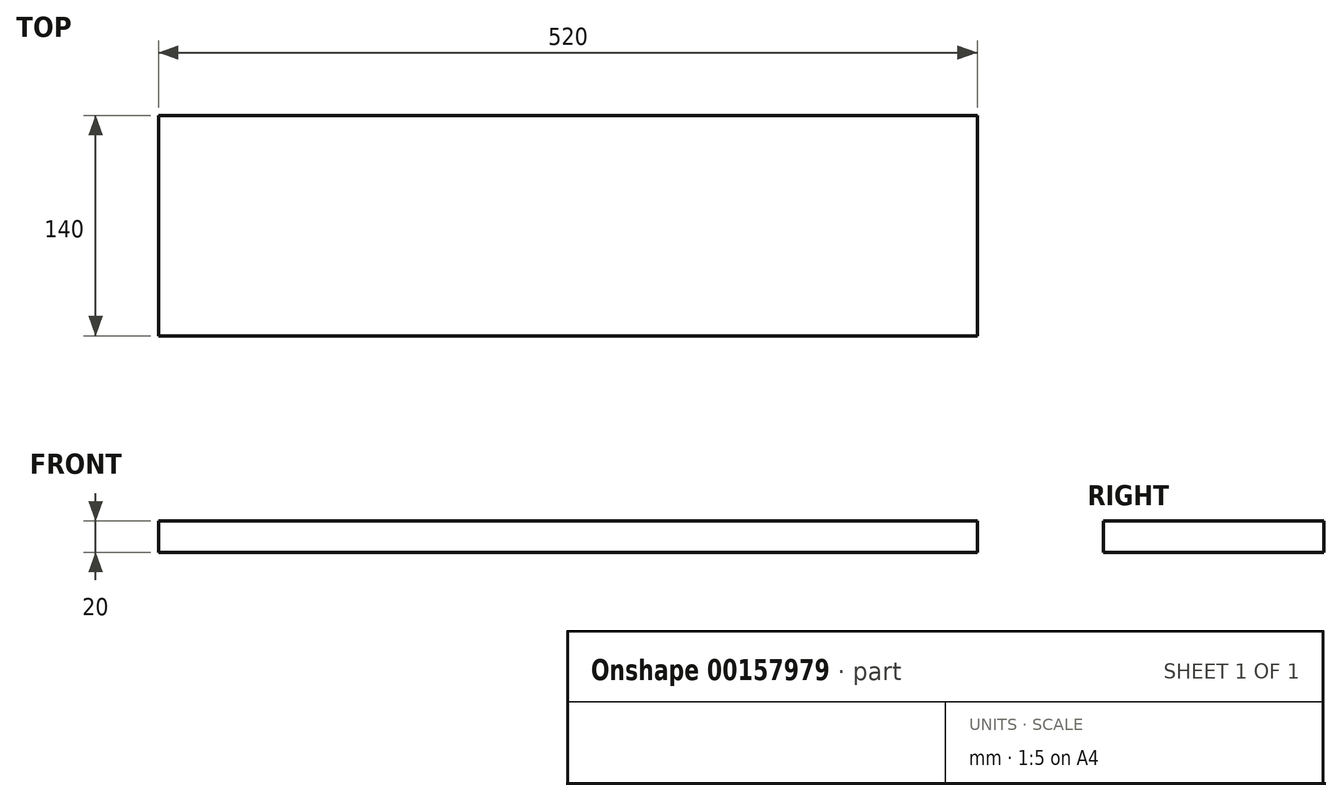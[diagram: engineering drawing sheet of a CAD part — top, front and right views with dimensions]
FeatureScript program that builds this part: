
annotation { "Feature Type Name" : "Feature", "Feature Type Description" : "" }
export const myFeature = defineFeature(function(context is Context, id is Id, definition is map)
    precondition{}
    {
        {
            var Q0;
            Q0=qCreatedBy(makeId("Top.planeOp"),FACE);
            var sketch = newSketch(context, id + "F0", { "sketchPlane" : qUnion([Q0])});
            skLineSegment(sketch, "E0.bottom", {"start": v(-260, -70) * mm, "end": v(260, -70) * mm});
            skLineSegment(sketch, "E0.top", {"start": v(-260, 70) * mm, "end": v(260, 70) * mm});
            skLineSegment(sketch, "E0.left", {"start": v(-260, -70) * mm, "end": v(-260, 70) * mm});
            skLineSegment(sketch, "E0.right", {"start": v(260, -70) * mm, "end": v(260, 70) * mm});
            skPoint(sketch, "E0.middle", {"position": v(0, 0) * mm});
            skSolve(sketch);
        }
        {
            var Q0;
            Q0=qSketchRegion(id+"F0",true);
            extrude(context, id + "F1", {"entities" : qUnion([Q0]), "endBound" : BoundingType.SYMMETRIC, "depth" : 20 * mm});
        }
    });
